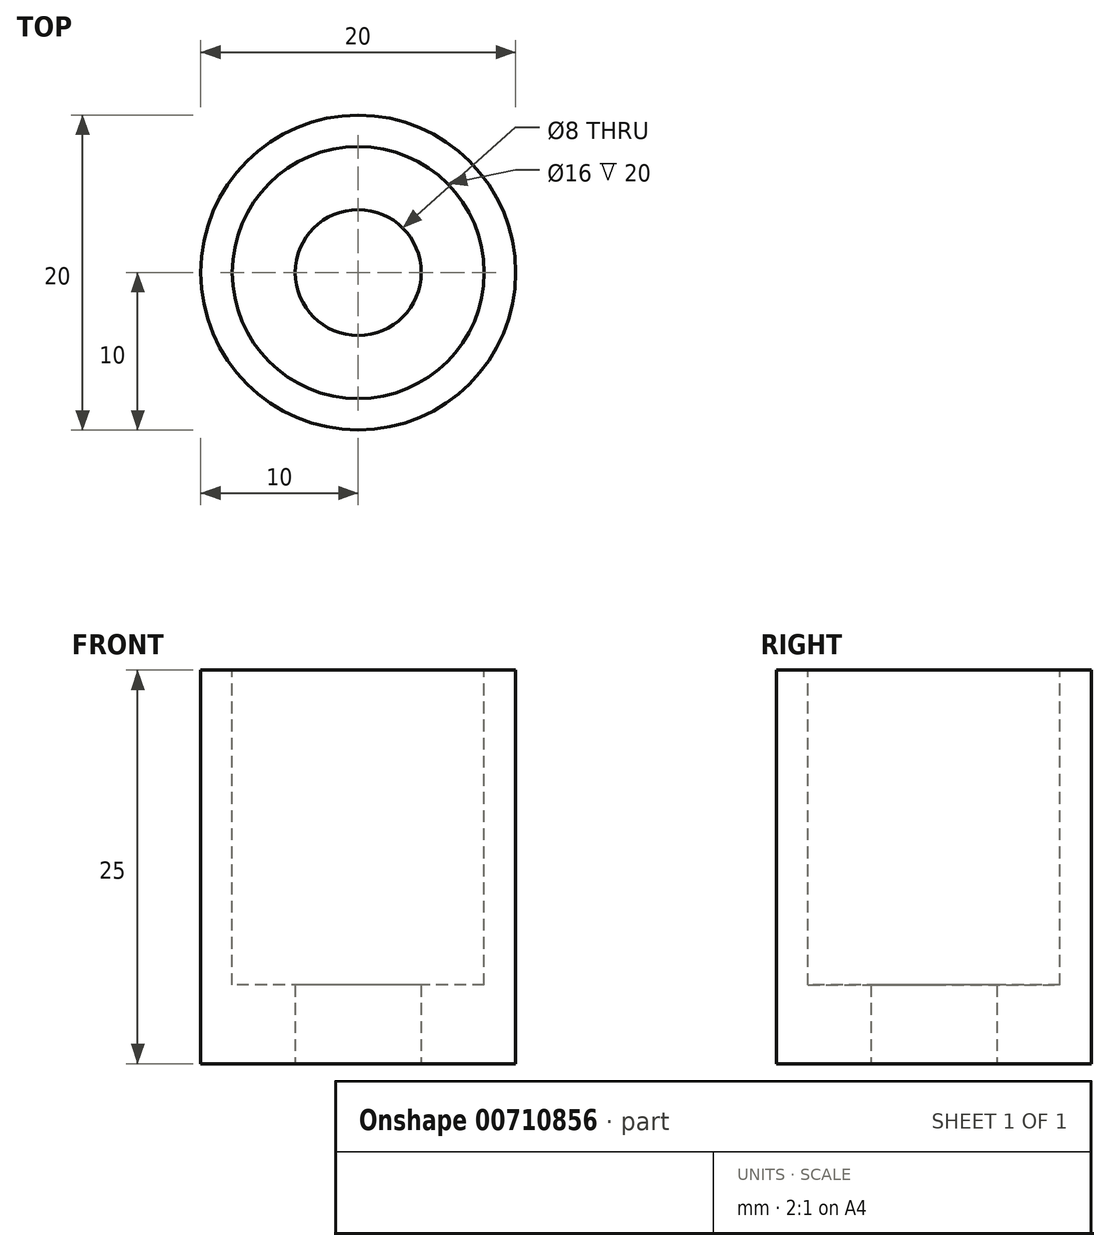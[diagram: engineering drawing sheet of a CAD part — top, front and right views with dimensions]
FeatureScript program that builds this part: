
annotation { "Feature Type Name" : "Feature", "Feature Type Description" : "" }
export const myFeature = defineFeature(function(context is Context, id is Id, definition is map)
    precondition{}
    {
        {
            var Q0;
            Q0=qCreatedBy(makeId("Top.planeOp"),FACE);
            var sketch = newSketch(context, id + "F0", { "sketchPlane" : qUnion([Q0])});
            skCircle(sketch, "E0", {"center": v(0, 0) * mm, "radius": 10 * mm});
            skCircle(sketch, "E1", {"center": v(0, 0) * mm, "radius": 4 * mm});
            skSolve(sketch);
        }
        {
            var Q0;
            Q0=qSketchRegion(id+"F0",true);
            extrude(context, id + "F1", {"entities" : qUnion([Q0]), "depth" : 25 * mm, "offsetDistance" : 25 * mm});
        }
        {
            var Q0;
            Q0=makeQuery(id+"F1.opExtrude","CAP_FACE",FACE,{"disambiguationData":[OSD([sQuery(id+"F0.wireOp",EDGE,"E0")])],"isStart":false});
            var sketch = newSketch(context, id + "F2", { "sketchPlane" : qUnion([Q0])});
            skCircle(sketch, "E2", {"center": v(0, 0) * mm, "radius": 8 * mm});
            skSolve(sketch);
        }
        {
            var Q0;
            Q0=qSketchRegion(id+"F2",true);
            extrude(context, id + "F3", {"entities" : qUnion([Q0]), "operationType" : NewBodyOperationType.REMOVE, "oppositeDirection" : true, "depth" : 20 * mm, "offsetDistance" : 25 * mm});
        }
        {
            var Q0;
            Q0=qSketchRegion(id+"F0",true);
            extrude(context, id + "F4", {"entities" : qUnion([Q0]), "operationType" : NewBodyOperationType.ADD, "depth" : 5 * mm, "offsetDistance" : 25 * mm});
        }
    });
